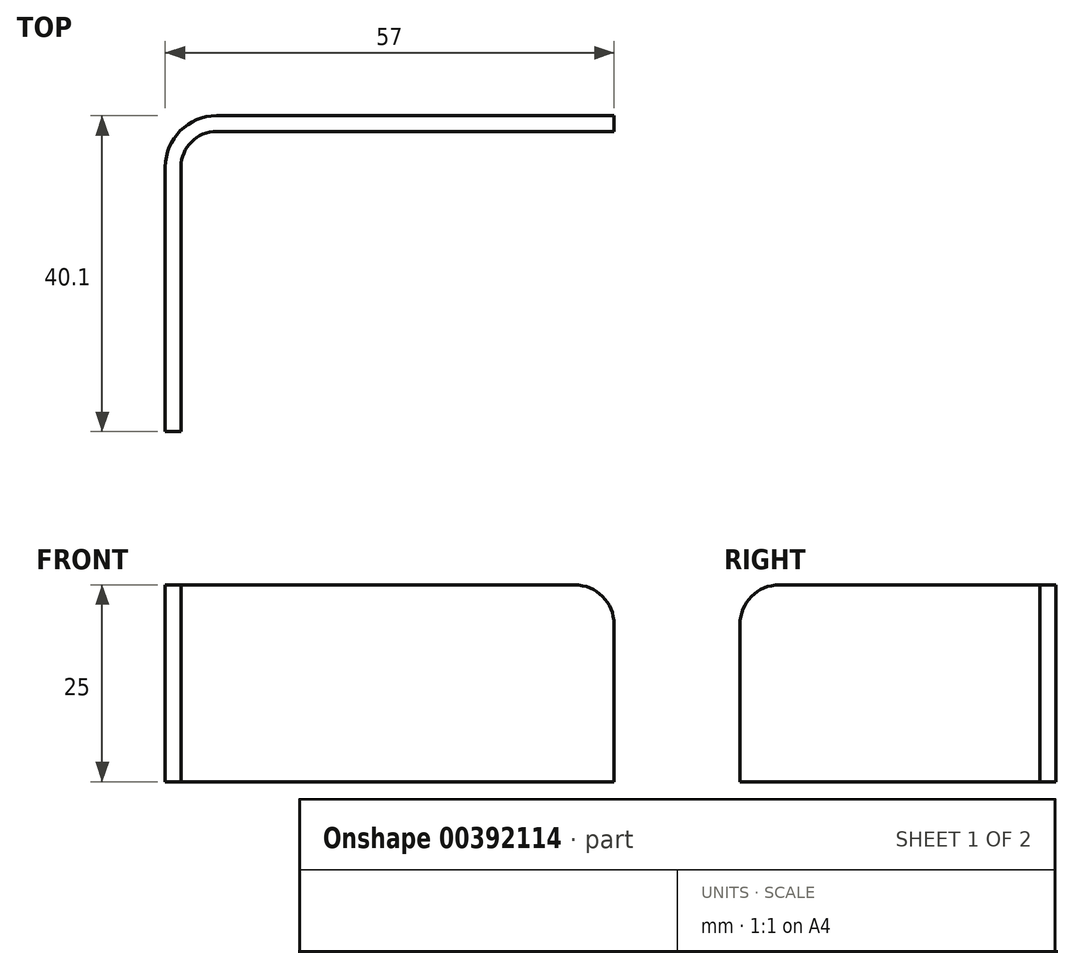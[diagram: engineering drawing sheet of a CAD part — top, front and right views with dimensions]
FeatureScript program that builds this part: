
annotation { "Feature Type Name" : "Feature", "Feature Type Description" : "" }
export const myFeature = defineFeature(function(context is Context, id is Id, definition is map)
    precondition{}
    {
        {
            var Q0;
            Q0=qCreatedBy(makeId("Top.planeOp"),FACE);
            var sketch = newSketch(context, id + "F0", { "sketchPlane" : qUnion([Q0])});
            skLineSegment(sketch, "E0.bottom", {"start": v(36.05, 21.3) * mm, "end": v(-36.05, 21.3) * mm});
            skLineSegment(sketch, "E0.top", {"start": v(36.05, -21.3) * mm, "end": v(-36.05, -21.3) * mm});
            skLineSegment(sketch, "E0.left", {"start": v(40.55, 16.8) * mm, "end": v(40.55, -16.8) * mm});
            skLineSegment(sketch, "E0.right", {"start": v(-40.55, 16.8) * mm, "end": v(-40.55, -16.8) * mm});
            skPoint(sketch, "E0.middle", {"position": v(0, 0) * mm});
            skArc(sketch, "E1.filletArc", {"start": v(-36.05, 21.3) * mm, "mid": v(-39.23, 19.98) * mm, "end": v(-40.55, 16.8) * mm});
            skPoint(sketch, "E2.visualSharp", {"position": v(40.55, 21.3) * mm});
            skArc(sketch, "E2.filletArc", {"start": v(40.55, 16.8) * mm, "mid": v(39.23, 19.98) * mm, "end": v(36.05, 21.3) * mm});
            skPoint(sketch, "E3.visualSharp", {"position": v(40.55, -21.3) * mm});
            skArc(sketch, "E3.filletArc", {"start": v(36.05, -21.3) * mm, "mid": v(39.23, -19.98) * mm, "end": v(40.55, -16.8) * mm});
            skPoint(sketch, "E4.visualSharp", {"position": v(-40.55, -21.3) * mm});
            skArc(sketch, "E4.filletArc", {"start": v(-40.55, -16.8) * mm, "mid": v(-39.23, -19.98) * mm, "end": v(-36.05, -21.3) * mm});
            skLineSegment(sketch, "E5", {"start": v(40.55, 0) * mm, "end": v(-40.55, 0) * mm, "construction": true});
            skLineSegment(sketch, "E6", {"start": v(0, 21.3) * mm, "end": v(0, -21.3) * mm, "construction": true});
            skLineSegment(sketch, "E7.bottom", {"start": v(-37.2, 14.05) * mm, "end": v(37.2, 14.05) * mm, "construction": true});
            skLineSegment(sketch, "E7.top", {"start": v(-37.2, -14.05) * mm, "end": v(37.2, -14.05) * mm, "construction": true});
            skLineSegment(sketch, "E7.left", {"start": v(-37.2, 14.05) * mm, "end": v(-37.2, -14.05) * mm, "construction": true});
            skLineSegment(sketch, "E7.right", {"start": v(37.2, 14.05) * mm, "end": v(37.2, -14.05) * mm, "construction": true});
            skPoint(sketch, "E8", {"position": v(37.2, 14.05) * mm});
            skPoint(sketch, "E9", {"position": v(37.2, -14.05) * mm});
            skPoint(sketch, "E10", {"position": v(-37.2, -14.05) * mm});
            skPoint(sketch, "E11", {"position": v(-37.2, 14.05) * mm});
            skLineSegment(sketch, "E12.0", {"start": v(-42.55, 16.8) * mm, "end": v(-42.55, -16.8) * mm});
            skArc(sketch, "E12.1", {"start": v(-36.05, 23.3) * mm, "mid": v(-40.65, 21.4) * mm, "end": v(-42.55, 16.8) * mm});
            skLineSegment(sketch, "E12.2", {"start": v(14.45, 23.3) * mm, "end": v(-36.05, 23.3) * mm});
            skLineSegment(sketch, "E13", {"start": v(-40.55, -16.8) * mm, "end": v(-42.55, -16.8) * mm});
            skLineSegment(sketch, "E14", {"start": v(14.45, 21.3) * mm, "end": v(14.45, 23.3) * mm});
            skSolve(sketch);
        }
        {
            var Q0;
            Q0=makeQuery(id+"F0.imprint","IMPRINT",FACE,{"disambiguationData":[TD([[makeQuery(id+"F0.imprint","IMPRINT",EDGE,{"derivedFrom":sQuery(id+"F0.wireOp",EDGE,"E0.right")}),-1.0]])]});
            extrude(context, id + "F1", {"entities" : qUnion([Q0]), "depth" : 25 * mm});
        }
        {
            var Q0;
            Q0=makeQuery(id+"F1.opExtrude","CAP_EDGE",EDGE,{"disambiguationData":[OSD([sQuery(id+"F0.wireOp",EDGE,"E13")])],"isStart":false});
            var Q1;
            Q1=makeQuery(id+"F1.opExtrude","CAP_EDGE",EDGE,{"disambiguationData":[OSD([sQuery(id+"F0.wireOp",EDGE,"E14")])],"isStart":false});
            fillet(context, id + "F2", {"entities" : qUnion([Q0, Q1]), "radius" : 5 * mm, "tangentPropagation" : true, "allowEdgeOverflow" : false});
        }
    });
